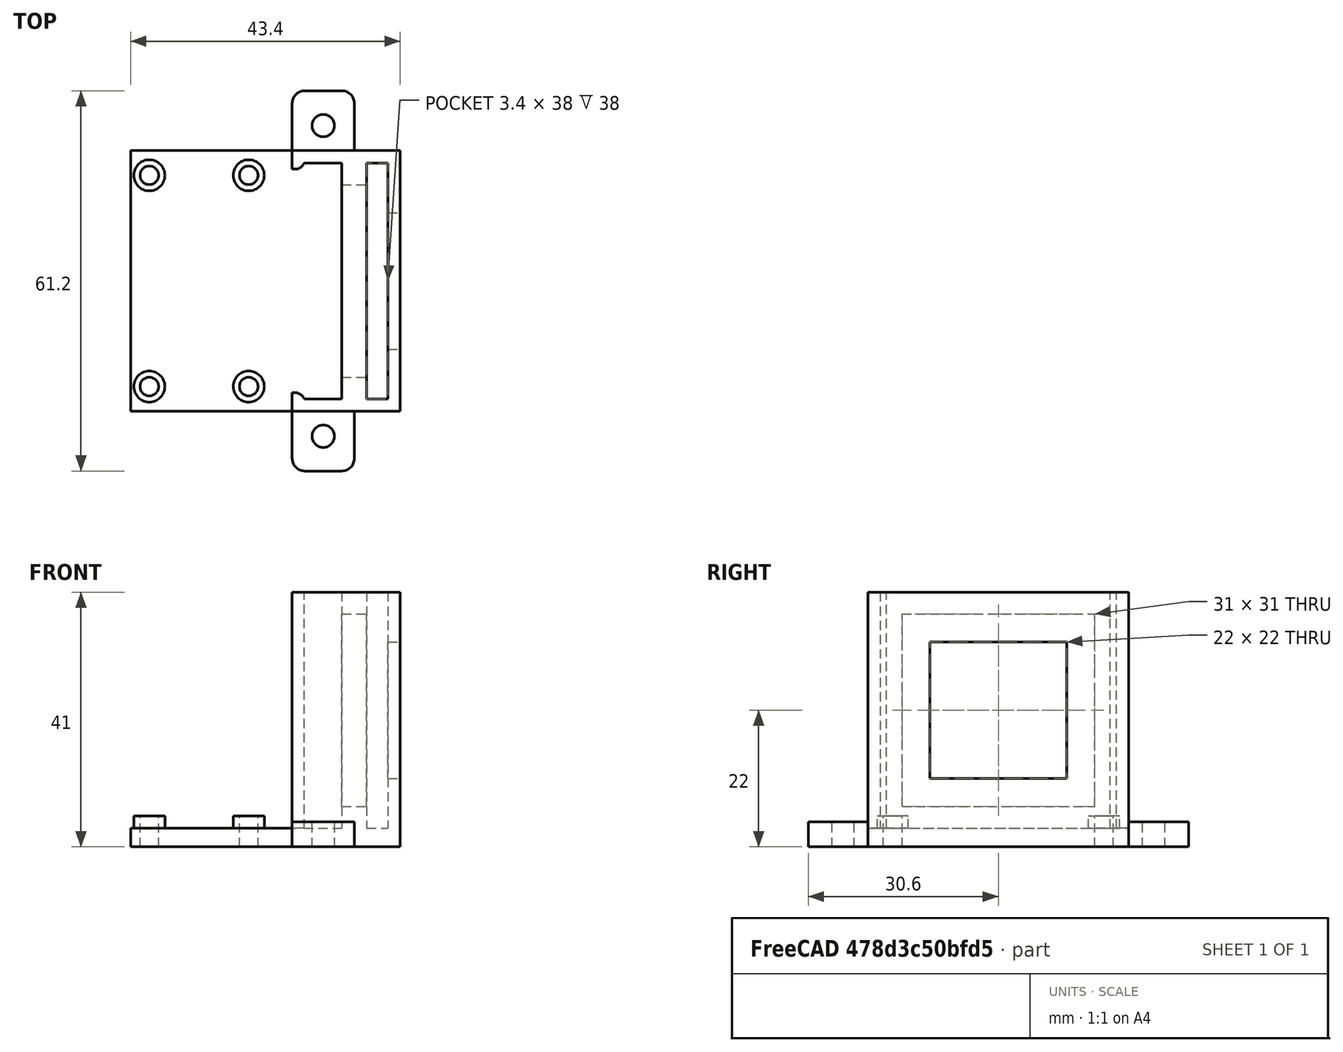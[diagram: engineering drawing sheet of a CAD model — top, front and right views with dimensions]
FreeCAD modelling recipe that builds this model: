
FCSTD DOCUMENT  (FreeCAD 0.18.4R)
Label: light_holder
License: All rights reserved
LicenseURL: http://en.wikipedia.org/wiki/All_rights_reserved
objects: Part::Box×8, Part::Cut×4, Part::Cylinder×3, Part::Fillet×2, Part::FeaturePython×2, Part::MultiFuse×2, Spreadsheet::Sheet×1, Part::Mirroring×1, App::Part×1
note: 22 computed .brp shape members not serialized (recipe doc carries the construction recipe); baked Part::Feature solids carry a one-line shape summary decoded from their .brp

FEATURE [Part::Box] Box  label="bottom cube"
  AttacherType = Attacher::AttachEngine3D
  Height = 3
  Length = 41.4
  Placement = pos=(-26,0,0) rot=(0,0,1;0rad)
  Width = 42
  expr: Placement.Base.x = -p.stepup_x - p.wall
  expr: Length = p.radiator_x + p.wall + p.stepup_x + 2 * p.wall + p.filter_x + p.wall
  expr: Width = p.radiator_y + 2 * p.wall
  expr: Height = p.under_pcb_plate_z
FEATURE [Spreadsheet::Sheet] Spreadsheet  label="p"
  cells = A1=wall; B1(wall)=2; A2=radiator_x; B2(radiator_x)=6; A3=radiator_y; B3(radiator_y)=38; A4=radiator_z; B4(radiator_z)=38; A5=stepup_x; B5(stepup_x)=24; A6=stepup_y; B6(stepup_y)=49; A7=stepup_under; B7(stepup_under)=2; A8=stepup_hole_dist_y; B8(stepup_hole_dist_y)=34; A9=stepup_hole_dist_x; B9(stepup_hole_dist_x)=16; A10=plate_hole_dist; B10(plate_hole_dist)=10; A11=under_pcb_plate_z; B11(under_pcb_plate_z)=3; A12=filter_x; B12(filter_x)=3.4; A13=light_wall_x; B13(light_wall_x)=4; A14=filter_wall_x; B14(filter_wall_x)=2; A15=filter_hole_y; B15(filter_hole_y)=22; A16=filter_hole_z; B16(filter_hole_z)=22; A17=light_hole_y; B17(light_hole_y)=31; A18=light_hole_z; B18(light_hole_z)=31
FEATURE [Part::Box] Box001  label="side cube"
  AttacherType = Attacher::AttachEngine3D
  Height = 41
  Length = 17.4
  Width = 2
  expr: Length = p.radiator_x + p.wall + p.light_wall_x + p.filter_x + p.filter_wall_x
  expr: Width = p.wall
  expr: Height = p.radiator_z + p.under_pcb_plate_z
FEATURE [Part::Box] Box002  label="light wall cube"
  AttacherType = Attacher::AttachEngine3D
  Height = 41
  Length = 4
  Placement = pos=(8,0,0) rot=(0,0,1;0rad)
  Width = 42
  expr: Placement.Base.x = p.radiator_x + p.wall
  expr: Length = p.light_wall_x
  expr: Width = p.radiator_y + 2 * p.wall
  expr: Height = p.radiator_z + p.under_pcb_plate_z
FEATURE [Part::Box] Box003  label="light wall hole cube"
  AttacherType = Attacher::AttachEngine3D
  Height = 31
  Length = 4
  Placement = pos=(8,5.5,6.5) rot=(0,0,1;0rad)
  Width = 31
  expr: Placement.Base.y = (2 * p.wall + p.radiator_y - p.light_hole_y) / 2
  expr: Placement.Base.x = p.radiator_x + p.wall
  expr: Length = p.light_wall_x
  expr: Width = p.light_hole_y
  expr: Placement.Base.z = p.under_pcb_plate_z + (p.radiator_z - p.light_hole_z) / 2
  expr: Height = p.light_hole_z
FEATURE [Part::Cut] Cut  label="light wall"
  Base = -> Box002
  Tool = -> Box003
FEATURE [Part::Box] Box004  label="bolt hole cube"
  AttacherType = Attacher::AttachEngine3D
  Height = 4
  Length = 10
  Placement = pos=(0,-9.6,0) rot=(0,0,1;0rad)
  Width = 9.6
  expr: Placement.Base.y = p.radiator_y / 2 + p.wall - 5 * p.plate_hole_dist / 2 - 3.6 - p.wall
  expr: Length = p.radiator_x + 2 * p.wall
  expr: Width = -p.radiator_y / 2 - p.wall + 5 * p.plate_hole_dist / 2 + 3.6 + p.wall
  expr: Height = p.wall + 2
FEATURE [Part::Cylinder] Cylinder001  label="bolt hole"
  Angle = 360
  AttacherType = Attacher::AttachEngine3D
  Height = 10
  Placement = pos=(5,-4,-3) rot=(0,0,1;0rad)
  Radius = 1.8
  expr: Placement.Base.y = p.radiator_y / 2 + p.wall - 5 * p.plate_hole_dist / 2
  expr: Placement.Base.x = (p.radiator_x + 2 * p.wall) / 2
FEATURE [Part::Box] Box005  label="side locker cube"
  AttacherType = Attacher::AttachEngine3D
  Height = 41
  Length = 2
  Width = 3
  expr: Length = p.wall
  expr: Width = p.wall + 1
  expr: Height = p.radiator_z + p.under_pcb_plate_z
FEATURE [Part::Fillet] Fillet  label="side locker fillet"
  Base = -> Box005
  Edges = 1 edges r=1.5: [Edge7]
FEATURE [Part::Cylinder] Cylinder  label="stepup_bolt_hole"
  Angle = 360
  AttacherType = Attacher::AttachEngine3D
  Height = 20
  Placement = pos=(-23,4,0) rot=(0,0,1;0rad)
  Radius = 1.5
FEATURE [Part::FeaturePython] Array  label="stepup bolt hole array"  # Draft array (typed FeaturePython)
  Angle = 360
  ArrayType = 0
  Axis = (0,0,1)
  Base = -> Cylinder
  Center = (0,0,0)
  Fuse = false
  IntervalAxis = (0,0,0)
  IntervalX = (16,0,0)
  IntervalY = (0,34,0)
  IntervalZ = (0,0,1)
  NumberPolar = 1
  NumberX = 2
  NumberY = 2
  NumberZ = 1
  expr: IntervalY.y = p.stepup_hole_dist_y
  expr: IntervalX.x = p.stepup_hole_dist_x
FEATURE [Part::Cylinder] Cylinder002  label="stepup_bolt_stand"
  Angle = 360
  AttacherType = Attacher::AttachEngine3D
  Height = 5
  Placement = pos=(-23,4,0) rot=(0,0,1;0rad)
  Radius = 2.5
  expr: Height = p.under_pcb_plate_z + p.stepup_under
FEATURE [Part::FeaturePython] Array001  label="stepup bolt stand array"  # Draft array (typed FeaturePython)
  Angle = 360
  ArrayType = 0
  Axis = (0,0,1)
  Base = -> Cylinder002
  Center = (0,0,0)
  Fuse = false
  IntervalAxis = (0,0,0)
  IntervalX = (16,0,0)
  IntervalY = (0,34,0)
  IntervalZ = (0,0,1)
  NumberPolar = 1
  NumberX = 2
  NumberY = 2
  NumberZ = 1
  expr: IntervalY.y = p.stepup_hole_dist_y
  expr: IntervalX.x = p.stepup_hole_dist_x
FEATURE [Part::Fillet] Fillet001  label="bolt hole cube fillet"
  Base = -> Box004
  Edges = 2 edges r=2: [Edge1,Edge5]
FEATURE [Part::MultiFuse] Fusion  label="side fusion"
  Shapes = -> [Box001,Fillet,Fillet001]
FEATURE [Part::Cut] Cut001  label="side cut"
  Base = -> Fusion
  Tool = -> Cylinder001
FEATURE [Part::Mirroring] Part__Mirroring  label="side cut (Mirror #1)"
  Base = (0,21,0)
  Normal = (0,1,0)
  Source = -> Cut001
  expr: Base.y = (p.radiator_y + 2 * p.wall) / 2
FEATURE [Part::Box] Box006  label="filter wall cube"
  AttacherType = Attacher::AttachEngine3D
  Height = 41
  Length = 2
  Placement = pos=(8,0,0) rot=(0,0,1;0rad)
  Width = 42
  expr: Placement.Base.x = p.radiator_x + p.wall
  expr: Length = p.filter_wall_x
  expr: Width = p.radiator_y + 2 * p.wall
  expr: Height = p.radiator_z + p.under_pcb_plate_z
FEATURE [Part::Box] Box007  label="filter wall hole cube"
  AttacherType = Attacher::AttachEngine3D
  Height = 22
  Length = 2
  Placement = pos=(8,10,11) rot=(0,0,1;0rad)
  Width = 22
  expr: Placement.Base.y = (2 * p.wall + p.radiator_y - p.filter_hole_y) / 2
  expr: Placement.Base.x = p.radiator_x + p.wall
  expr: Length = p.wall
  expr: Width = p.filter_hole_y
  expr: Placement.Base.z = p.under_pcb_plate_z + (p.radiator_z - p.filter_hole_z) / 2
  expr: Height = p.filter_hole_z
FEATURE [Part::Cut] Cut003  label="filter wall"
  Base = -> Box006
  Placement = pos=(7.4,0,0) rot=(0,0,1;0rad)
  Tool = -> Box007
  expr: Placement.Base.x = p.light_wall_x + p.filter_x
FEATURE [Part::MultiFuse] Fusion001  label="light holder fusion"
  Shapes = -> [Array001,Cut001,Box,Part__Mirroring,Cut,Cut003]
FEATURE [Part::Cut] Cut002  label="lighter holder cut"
  Base = -> Fusion001
  Tool = -> Array
FEATURE [App::Part] Part  label="light holder part"
  Group = -> [Cut,Cut001,Box002,Box001,Part__Mirroring,Cylinder001,Box003,Box004,Box,Fusion,Fillet,Box005,Array001,Cylinder002,Fusion001,Array,Cylinder,Cut002]
  Origin = -> Origin
